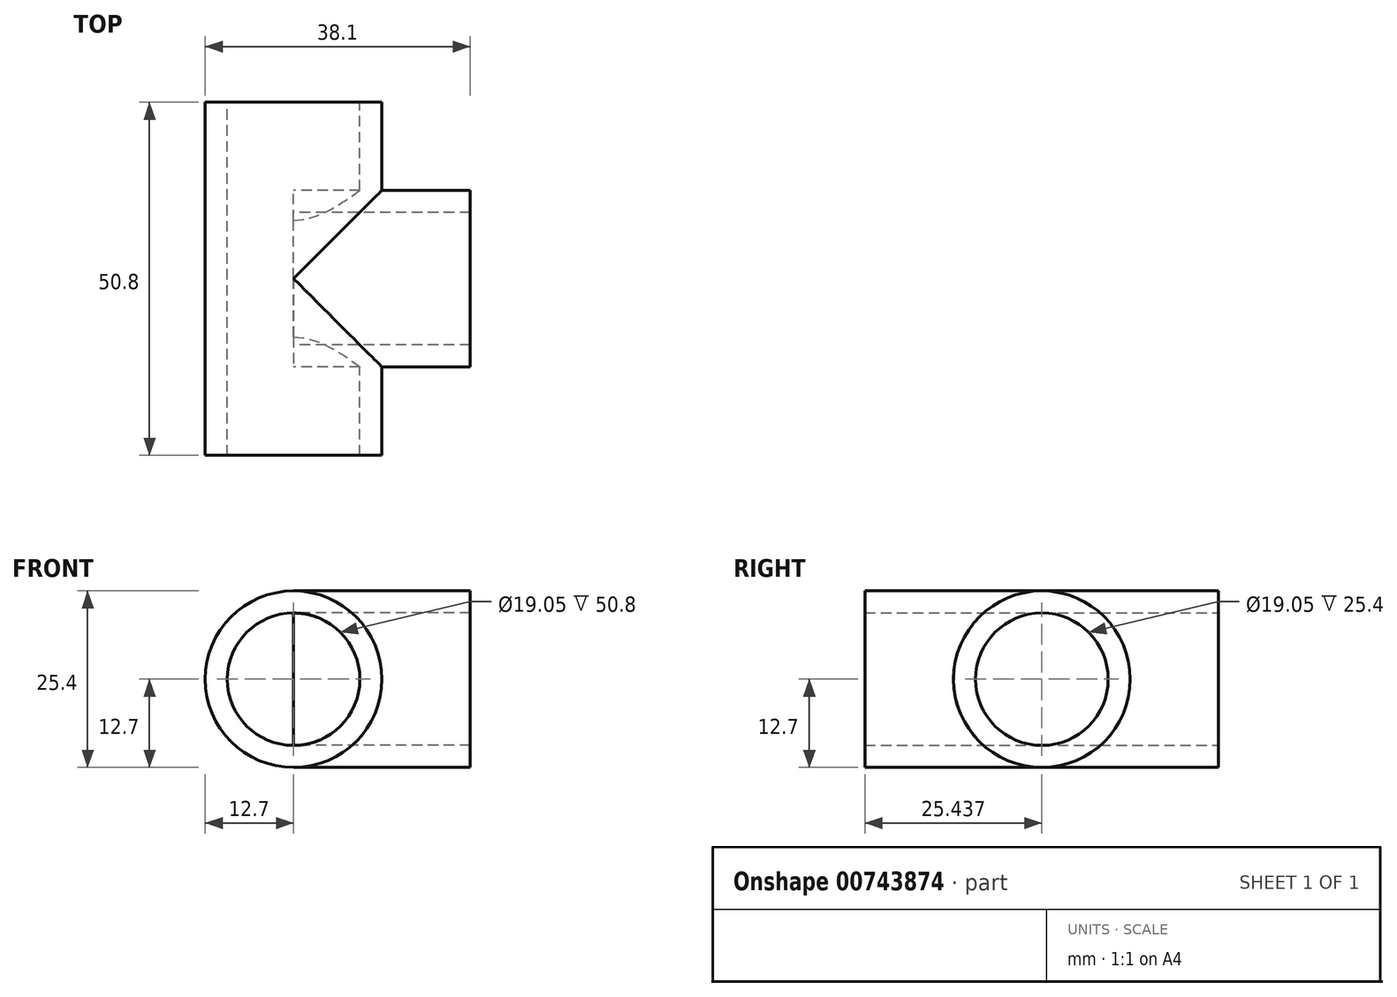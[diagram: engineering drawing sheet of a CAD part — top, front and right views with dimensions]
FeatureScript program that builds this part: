
annotation { "Feature Type Name" : "Feature", "Feature Type Description" : "" }
export const myFeature = defineFeature(function(context is Context, id is Id, definition is map)
    precondition{}
    {
        {
            var Q0;
            Q0=qCreatedBy(makeId("Front.planeOp"),FACE);
            var sketch = newSketch(context, id + "F0", { "sketchPlane" : qUnion([Q0])});
            skCircle(sketch, "E0", {"center": v(0, 0) * mm, "radius": 9.53 * mm});
            skCircle(sketch, "E1", {"center": v(0, 0) * mm, "radius": 12.7 * mm});
            skSolve(sketch);
        }
        {
            var Q0;
            Q0 = qSketchRegion(id + "F0", true);
            extrude(context, id + "F1", {"entities" : qUnion([Q0]), "depth" : 50.8 * mm, "offsetDistance" : 25.4 * mm});
        }
        {
            var Q0;
            Q0=qCreatedBy(makeId("Right.planeOp"),FACE);
            var sketch = newSketch(context, id + "F2", { "sketchPlane" : qUnion([Q0])});
            skCircle(sketch, "E2", {"center": v(-25.36, 0) * mm, "radius": 12.7 * mm});
            skSolve(sketch);
        }
        {
            var Q0;
            Q0=qCreatedBy(makeId("Right.planeOp"),FACE);
            var sketch = newSketch(context, id + "F3", { "sketchPlane" : qUnion([Q0])});
            skCircle(sketch, "E3", {"center": v(-25.36, 0) * mm, "radius": 9.53 * mm});
            skSolve(sketch);
        }
        {
            var Q0;
            Q0=makeQuery(id+"F2.imprint","IMPRINT",FACE,{"disambiguationData":[TD([[makeQuery(id+"F2.imprint","IMPRINT",EDGE,{"derivedFrom":sQuery(id+"F2.wireOp",EDGE,"E2")}),1.0]])]});
            extrude(context, id + "F4", {"entities" : qUnion([Q0]), "operationType" : NewBodyOperationType.ADD, "depth" : 25.4 * mm, "offsetDistance" : 25.4 * mm});
        }
        {
            var Q0;
            Q0 = qSketchRegion(id + "F3", true);
            extrude(context, id + "F5", {"entities" : qUnion([Q0]), "operationType" : NewBodyOperationType.REMOVE, "depth" : 25.4 * mm, "offsetDistance" : 25.4 * mm});
        }
    });
